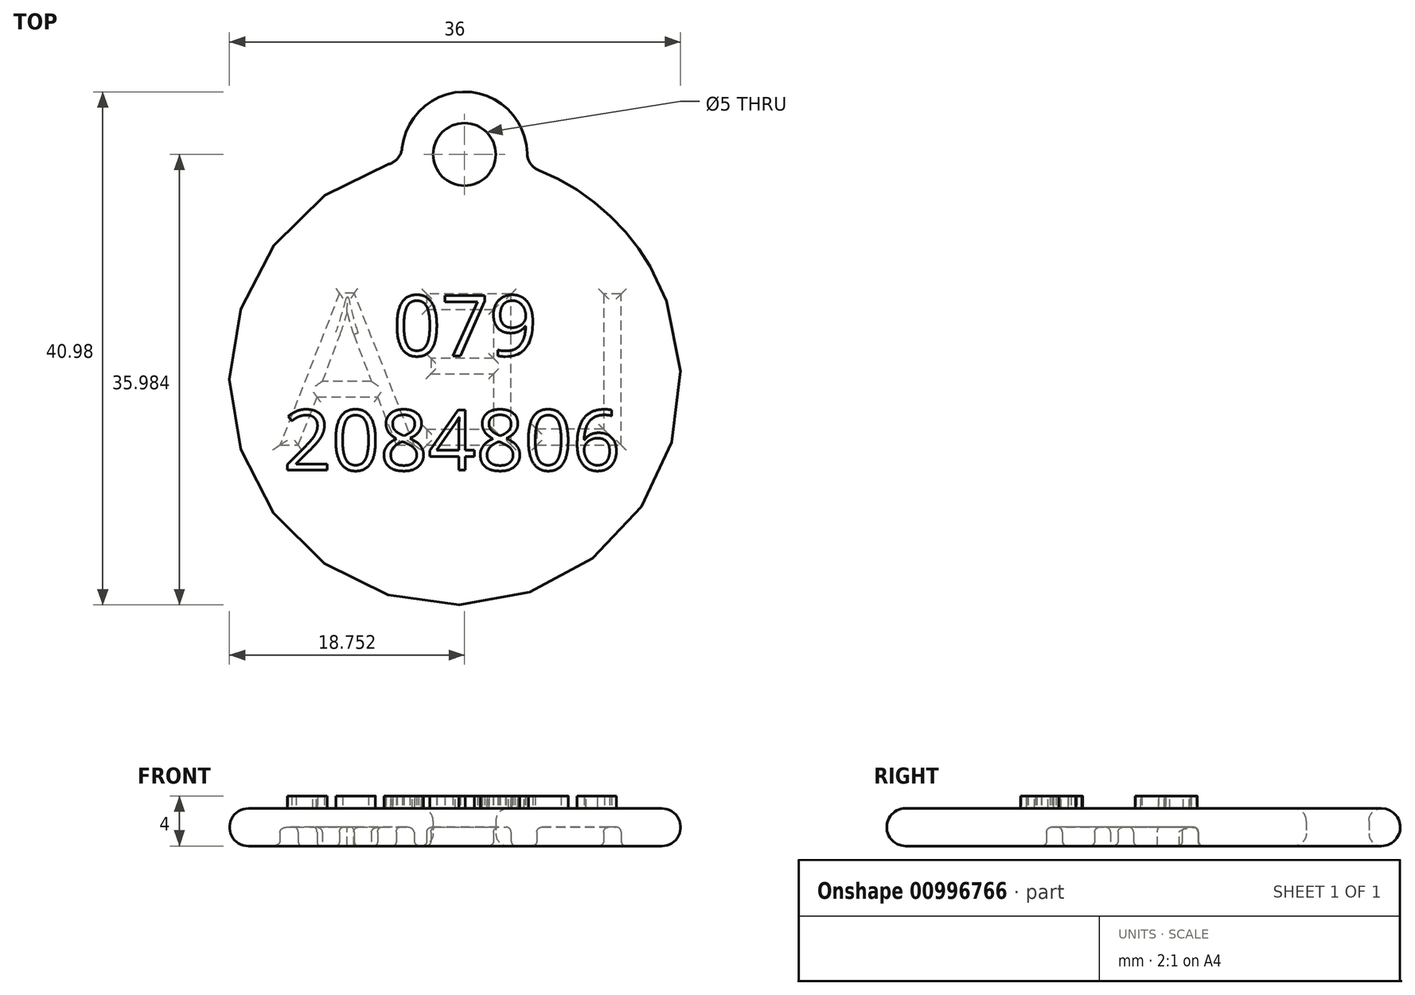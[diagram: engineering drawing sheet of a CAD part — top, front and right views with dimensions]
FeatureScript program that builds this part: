
annotation { "Feature Type Name" : "Feature", "Feature Type Description" : "" }
export const myFeature = defineFeature(function(context is Context, id is Id, definition is map)
    precondition{}
    {
        {
            var Q0;
            Q0=qCreatedBy(makeId("Top.planeOp"),FACE);
            var sketch = newSketch(context, id + "F0", { "sketchPlane" : qUnion([Q0])});
            skArc(sketch, "E0", {"start": v(-4.22, 17.5) * mm, "mid": v(-0.75, -17.98) * mm, "end": v(5.67, 17.08) * mm});
            skArc(sketch, "E1", {"start": v(5.67, 17.08) * mm, "mid": v(0.96, 22.98) * mm, "end": v(-4.22, 17.5) * mm});
            skCircle(sketch, "E2", {"center": v(0.75, 17.98) * mm, "radius": 2.5 * mm});
            skSolve(sketch);
        }
        {
            var Q0;
            Q0=makeQuery(id+"F0.imprint","IMPRINT",FACE,{"disambiguationData":[TD([[makeQuery(id+"F0.imprint","IMPRINT",EDGE,{"derivedFrom":sQuery(id+"F0.wireOp",EDGE,"E0")}),1.0]])]});
            extrude(context, id + "F1", {"entities" : qUnion([Q0]), "depth" : 3 * mm, "offsetDistance" : 25 * mm});
        }
        {
            var Q0;
            Q0=makeQuery(id+"F1.opExtrude","SWEPT_FACE",FACE,{"disambiguationData":[OSD([sQuery(id+"F0.wireOp",EDGE,"E1")])]});
            var Q1;
            Q1=makeQuery(id+"F1.opExtrude","SWEPT_FACE",FACE,{"disambiguationData":[OSD([sQuery(id+"F0.wireOp",EDGE,"E0")])]});
            fillet(context, id + "F2", {"entities" : qUnion([Q0, Q1]), "radius" : 1.5 * mm, "tangentPropagation" : true, "allowEdgeOverflow" : false});
        }
        {
            var Q0;
            Q0=makeQuery(id+"F1.opExtrude","CAP_EDGE",EDGE,{"disambiguationData":[OSD([sQuery(id+"F0.wireOp",EDGE,"E2")])],"isStart":false});
            fillet(context, id + "F3", {"entities" : qUnion([Q0]), "radius" : 1 * mm, "tangentPropagation" : true, "allowEdgeOverflow" : false});
        }
        {
            var Q0;
            Q0=makeQuery(id+"F1.opExtrude","CAP_EDGE",EDGE,{"disambiguationData":[OSD([sQuery(id+"F0.wireOp",EDGE,"E2")])],"isStart":true});
            fillet(context, id + "F4", {"entities" : qUnion([Q0]), "radius" : 1 * mm, "tangentPropagation" : true, "allowEdgeOverflow" : false});
        }
        {
            var Q0;
            Q0=makeQuery(id+"F1.opExtrude","CAP_FACE",FACE,{"disambiguationData":[OSD([sQuery(id+"F0.wireOp",EDGE,"E0"),sQuery(id+"F0.wireOp",EDGE,"E1"),sQuery(id+"F0.wireOp",EDGE,"E2")])],"isStart":false});
            var sketch = newSketch(context, id + "F5", { "sketchPlane" : qUnion([Q0])});
            skText(sketch, "E3", { "text": "     079\n2084806", "fontName": "OpenSans-Regular.ttf"});
            const initialGuessF5  = {"E3": [-0.0137, 0.0019, 1, 0, 0.00484]};
            skSetInitialGuess(sketch, initialGuessF5);
            skSolve(sketch);
        }
        {
            var Q0;
            Q0 = qSketchRegion(id + "F5", true);
            extrude(context, id + "F6", {"entities" : qUnion([Q0]), "operationType" : NewBodyOperationType.ADD, "depth" : 1 * mm, "offsetDistance" : 25 * mm});
        }
        {
            var Q0;
            Q0=makeQuery(id+"F1.opExtrude","CAP_FACE",FACE,{"disambiguationData":[OSD([sQuery(id+"F0.wireOp",EDGE,"E0"),sQuery(id+"F0.wireOp",EDGE,"E1"),sQuery(id+"F0.wireOp",EDGE,"E2")])],"isStart":true});
            var sketch = newSketch(context, id + "F7", { "sketchPlane" : qUnion([Q0])});
            skText(sketch, "E4", { "text": "LEA\n", "fontName": "OpenSans-Regular.ttf"});
            const initialGuessF7  = {"E4": [0.01492, 0.00524, -1, 0, 0.01218]};
            skSetInitialGuess(sketch, initialGuessF7);
            skSolve(sketch);
        }
        {
            var Q0;
            Q0 = qSketchRegion(id + "F7", true);
            extrude(context, id + "F8", {"entities" : qUnion([Q0]), "operationType" : NewBodyOperationType.REMOVE, "oppositeDirection" : true, "depth" : 1.5 * mm, "offsetDistance" : 25 * mm});
        }
        {
            var Q0;
            Q0=makeQuery(id+"F8.boolean.opBoolean","COPY",FACE,{"derivedFrom":makeQuery(id+"F8.opExtrude","CAP_FACE",FACE,{"disambiguationData":[OSD([sQuery(id+"F7.wireOp",EDGE,"E4.sketch_text.stroke-18"),sQuery(id+"F7.wireOp",EDGE,"E4.sketch_text.stroke-19"),sQuery(id+"F7.wireOp",EDGE,"E4.sketch_text.stroke-20"),sQuery(id+"F7.wireOp",EDGE,"E4.sketch_text.stroke-21"),sQuery(id+"F7.wireOp",EDGE,"E4.sketch_text.stroke-22"),sQuery(id+"F7.wireOp",EDGE,"E4.sketch_text.stroke-23"),sQuery(id+"F7.wireOp",EDGE,"E4.sketch_text.stroke-24"),sQuery(id+"F7.wireOp",EDGE,"E4.sketch_text.stroke-25"),sQuery(id+"F7.wireOp",EDGE,"E4.sketch_text.stroke-26"),sQuery(id+"F7.wireOp",EDGE,"E4.sketch_text.stroke-27"),sQuery(id+"F7.wireOp",EDGE,"E4.sketch_text.stroke-28"),sQuery(id+"F7.wireOp",EDGE,"E4.sketch_text.stroke-29"),sQuery(id+"F7.wireOp",EDGE,"E4.sketch_text.stroke-30")])],"isStart":false})});
            fillet(context, id + "F9", {"entities" : qUnion([Q0]), "radius" : 0.4 * mm, "tangentPropagation" : true, "allowEdgeOverflow" : false});
        }
        {
            var Q0;
            Q0=makeQuery(id+"F8.boolean.opBoolean","COPY",FACE,{"derivedFrom":makeQuery(id+"F8.opExtrude","CAP_FACE",FACE,{"disambiguationData":[OSD([sQuery(id+"F7.wireOp",EDGE,"E4.sketch_text.stroke-0"),sQuery(id+"F7.wireOp",EDGE,"E4.sketch_text.stroke-1"),sQuery(id+"F7.wireOp",EDGE,"E4.sketch_text.stroke-2"),sQuery(id+"F7.wireOp",EDGE,"E4.sketch_text.stroke-3"),sQuery(id+"F7.wireOp",EDGE,"E4.sketch_text.stroke-4"),sQuery(id+"F7.wireOp",EDGE,"E4.sketch_text.stroke-5")])],"isStart":false})});
            var Q1;
            Q1=makeQuery(id+"F8.boolean.opBoolean","COPY",FACE,{"derivedFrom":makeQuery(id+"F8.opExtrude","CAP_FACE",FACE,{"disambiguationData":[OSD([sQuery(id+"F7.wireOp",EDGE,"E4.sketch_text.stroke-6"),sQuery(id+"F7.wireOp",EDGE,"E4.sketch_text.stroke-7"),sQuery(id+"F7.wireOp",EDGE,"E4.sketch_text.stroke-8"),sQuery(id+"F7.wireOp",EDGE,"E4.sketch_text.stroke-9"),sQuery(id+"F7.wireOp",EDGE,"E4.sketch_text.stroke-10"),sQuery(id+"F7.wireOp",EDGE,"E4.sketch_text.stroke-11"),sQuery(id+"F7.wireOp",EDGE,"E4.sketch_text.stroke-12"),sQuery(id+"F7.wireOp",EDGE,"E4.sketch_text.stroke-13"),sQuery(id+"F7.wireOp",EDGE,"E4.sketch_text.stroke-14"),sQuery(id+"F7.wireOp",EDGE,"E4.sketch_text.stroke-15"),sQuery(id+"F7.wireOp",EDGE,"E4.sketch_text.stroke-16"),sQuery(id+"F7.wireOp",EDGE,"E4.sketch_text.stroke-17")])],"isStart":false})});
            var Q2;
            {var subQ0=sQuery(id+"F0.wireOp",EDGE,"E1");var subQ1=sQuery(id+"F0.wireOp",EDGE,"E2");var subQ2=sQuery(id+"F0.wireOp",EDGE,"E0");Q2=makeQuery(id+"F8.boolean.opBoolean","SPLIT",FACE,{"disambiguationData":[TD([makeQuery(id+"F2.opFillet","BLEND_FACE",FACE,{"disambiguationData":[OSD([subQ2])]})])],"derivedFrom":makeQuery(id+"F1.opExtrude","CAP_FACE",FACE,{"disambiguationData":[OSD([subQ2,subQ0,subQ1])],"isStart":true})});}
            fillet(context, id + "F10", {"entities" : qUnion([Q0, Q1, Q2]), "radius" : 0.4 * mm, "tangentPropagation" : true, "allowEdgeOverflow" : false});
        }
    });
